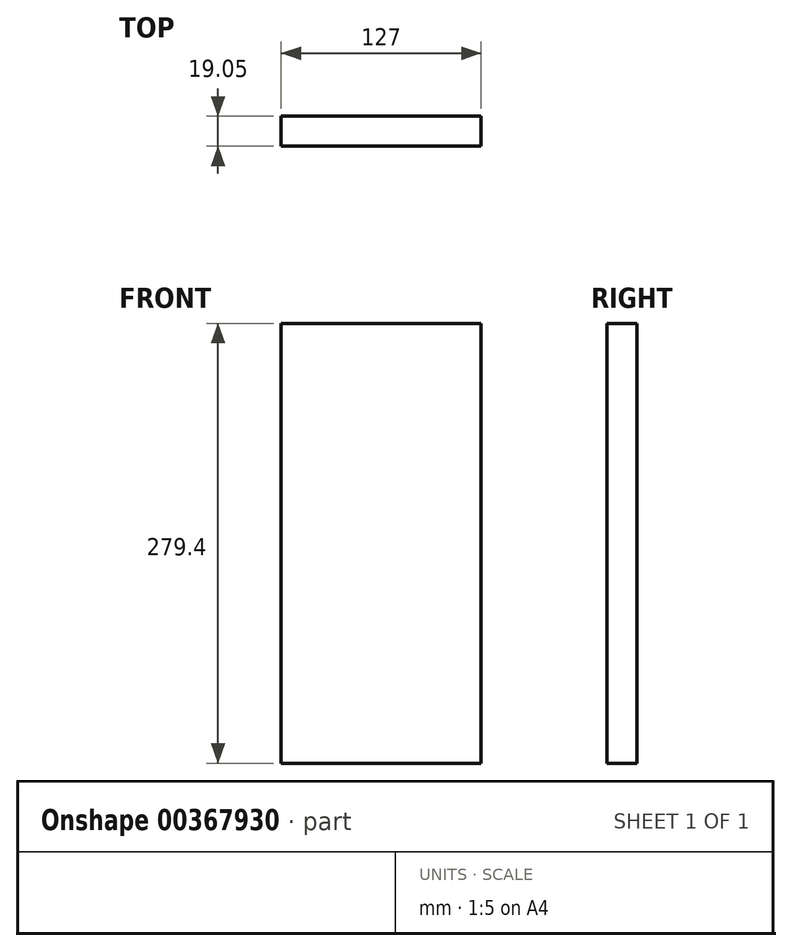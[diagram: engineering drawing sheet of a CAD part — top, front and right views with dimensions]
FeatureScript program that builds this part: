
annotation { "Feature Type Name" : "Feature", "Feature Type Description" : "" }
export const myFeature = defineFeature(function(context is Context, id is Id, definition is map)
    precondition{}
    {
        {
            var Q0;
            Q0=qCreatedBy(makeId("Front.planeOp"),FACE);
            var sketch = newSketch(context, id + "F0", { "sketchPlane" : qUnion([Q0])});
            skLineSegment(sketch, "E0.bottom", {"start": v(-89.35, 180.6) * mm, "end": v(37.65, 180.6) * mm});
            skLineSegment(sketch, "E0.top", {"start": v(-89.35, -98.8) * mm, "end": v(37.65, -98.8) * mm});
            skLineSegment(sketch, "E0.left", {"start": v(-89.35, 180.6) * mm, "end": v(-89.35, -98.8) * mm});
            skLineSegment(sketch, "E0.right", {"start": v(37.65, 180.6) * mm, "end": v(37.65, -98.8) * mm});
            skSolve(sketch);
        }
        {
            var Q0;
            Q0=makeQuery(id+"F0.imprint","IMPRINT",FACE,{"disambiguationData":[TD([[makeQuery(id+"F0.imprint","IMPRINT",EDGE,{"derivedFrom":sQuery(id+"F0.wireOp",EDGE,"E0.bottom")}),-1.0]])]});
            extrude(context, id + "F1", {"entities" : qUnion([Q0]), "depth" : 19.05 * mm});
        }
    });
